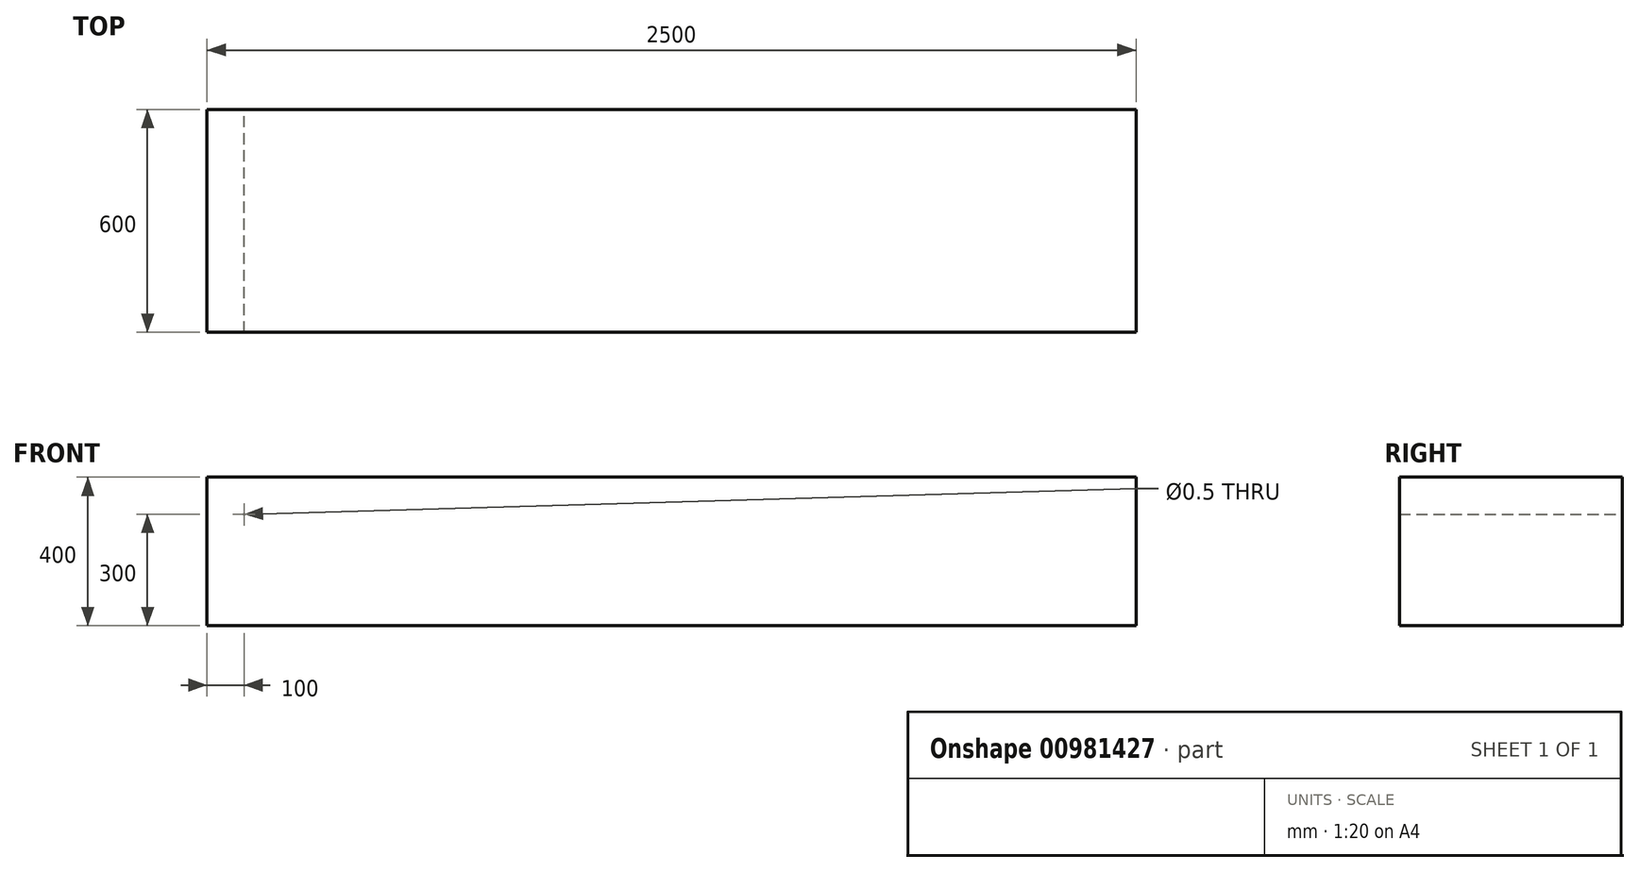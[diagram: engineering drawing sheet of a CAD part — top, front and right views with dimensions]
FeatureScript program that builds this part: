
annotation { "Feature Type Name" : "Feature", "Feature Type Description" : "" }
export const myFeature = defineFeature(function(context is Context, id is Id, definition is map)
    precondition{}
    {
        {
            var Q0;
            Q0=qCreatedBy(makeId("Top.planeOp"),FACE);
            var sketch = newSketch(context, id + "F0", { "sketchPlane" : qUnion([Q0])});
            skLineSegment(sketch, "E0.bottom", {"start": v(-1250, 300) * mm, "end": v(1250, 300) * mm});
            skLineSegment(sketch, "E0.top", {"start": v(-1250, -300) * mm, "end": v(1250, -300) * mm});
            skLineSegment(sketch, "E0.left", {"start": v(-1250, 300) * mm, "end": v(-1250, -300) * mm});
            skLineSegment(sketch, "E0.right", {"start": v(1250, 300) * mm, "end": v(1250, -300) * mm});
            skPoint(sketch, "E0.middle", {"position": v(0, 0) * mm});
            skSolve(sketch);
        }
        {
            var Q0;
            Q0 = qSketchRegion(id + "F0", true);
            extrude(context, id + "F1", {"entities" : qUnion([Q0]), "depth" : 400 * mm, "offsetDistance" : 25 * mm});
        }
        {
            var Q0;
            Q0=makeQuery(id+"F1.opExtrude","SWEPT_FACE",FACE,{"disambiguationData":[OSD([sQuery(id+"F0.wireOp",EDGE,"E0.bottom")])]});
            cPlane(context, id + "F2", {"entities" : qUnion([Q0]), "cplaneType" : CPlaneType.OFFSET, "offset" : 0 * mm, "width" : 150 * mm, "height" : 150 * mm});
        }
        {
            var Q0;
            Q0=qCreatedBy(id+"F2.planeOp",FACE);
            var sketch = newSketch(context, id + "F3", { "sketchPlane" : qUnion([Q0])});
            skPoint(sketch, "E1", {"position": v(1150, 300) * mm});
            skSolve(sketch);
        }
        {
            var Q0;
            Q0=sQuery(id+"F3.wireOp",VERTEX,"E1");
            var Q1;
            Q1=makeQuery(id+"F1.opExtrude","SWEPT_BODY",BODY,{"disambiguationData":[OSD([sQuery(id+"F0.wireOp",EDGE,"E0.bottom"),sQuery(id+"F0.wireOp",EDGE,"E0.top"),sQuery(id+"F0.wireOp",EDGE,"E0.left"),sQuery(id+"F0.wireOp",EDGE,"E0.right")])]});
            hole(context, id + "F4", {"style" : HoleStyle.SIMPLE, "endStyle" : HoleEndStyle.THROUGH, "holeDiameter" : 0.5 * mm, "majorDiameter" : 5 * mm, "isTappedThrough" : true, "tappedDepth" : 12 * mm, "tapClearance" : 3, "startFromSketch" : true, "locations" : qUnion([Q0]), "scope" : qUnion([Q1])});
        }
    });
